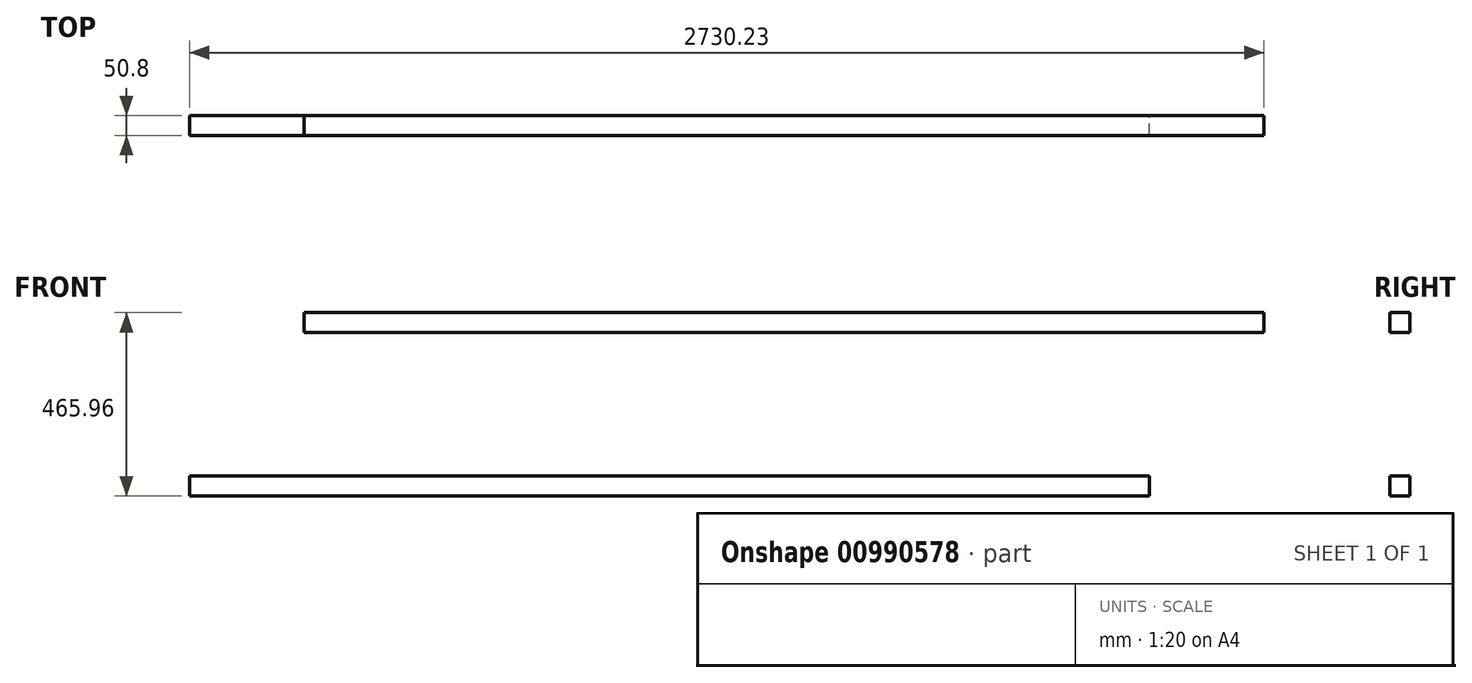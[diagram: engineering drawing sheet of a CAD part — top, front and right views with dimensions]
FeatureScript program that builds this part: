
annotation { "Feature Type Name" : "Feature", "Feature Type Description" : "" }
export const myFeature = defineFeature(function(context is Context, id is Id, definition is map)
    precondition{}
    {
        {
            var Q0;
            Q0=qCreatedBy(makeId("Front.planeOp"),FACE);
            var sketch = newSketch(context, id + "F0", { "sketchPlane" : qUnion([Q0])});
            skLineSegment(sketch, "E0.bottom", {"start": v(-506.88, -148.1) * mm, "end": v(1931.52, -148.1) * mm});
            skLineSegment(sketch, "E0.top", {"start": v(-506.88, -198.9) * mm, "end": v(1931.52, -198.9) * mm});
            skLineSegment(sketch, "E0.left", {"start": v(-506.88, -148.1) * mm, "end": v(-506.88, -198.9) * mm});
            skLineSegment(sketch, "E0.right", {"start": v(1931.52, -148.1) * mm, "end": v(1931.52, -198.9) * mm});
            skLineSegment(sketch, "E1.bottom", {"start": v(-215.05, 267.07) * mm, "end": v(2223.35, 267.07) * mm});
            skLineSegment(sketch, "E1.top", {"start": v(-215.05, 216.27) * mm, "end": v(2223.35, 216.27) * mm});
            skLineSegment(sketch, "E1.left", {"start": v(-215.05, 267.07) * mm, "end": v(-215.05, 216.27) * mm});
            skLineSegment(sketch, "E1.right", {"start": v(2223.35, 267.07) * mm, "end": v(2223.35, 216.27) * mm});
            skSolve(sketch);
        }
        {
            var Q0;
            Q0=makeQuery(id+"F0.imprint","IMPRINT",FACE,{"disambiguationData":[TD([[makeQuery(id+"F0.imprint","IMPRINT",EDGE,{"derivedFrom":sQuery(id+"F0.wireOp",EDGE,"E1.bottom")}),-1.0]])]});
            var Q1;
            Q1=makeQuery(id+"F0.imprint","IMPRINT",FACE,{"disambiguationData":[TD([[makeQuery(id+"F0.imprint","IMPRINT",EDGE,{"derivedFrom":sQuery(id+"F0.wireOp",EDGE,"E0.bottom")}),-1.0]])]});
            extrude(context, id + "F1", {"entities" : qUnion([Q0, Q1]), "depth" : 50.8 * mm, "offsetDistance" : 25.4 * mm});
        }
    });
